# Revit family: QUADRATE NEON FLEX 1312_NDFX35_UU.1_N.1
name_source: partatom
category: Luminarias
units: mm (PartAtom-declared; Revit-internal decimal feet)

## family parameters
Compartido = No
Corte con vacíos al cargar = No
Cota de conector redondo = Diámetro de uso
Origen de luz = Sí
Punto de cálculo de habitación = No
Se basa en plano de trabajo = Sí
Siempre vertical = No
Tipo de pieza = Normal

## types (1)
- QUADRATENEON FLEX 1312_NDFX35.UU.1
    Cambio de temperatura de color de luz atenuada = <Ninguno>
    Comentarios de vataje = 24
    Descripción = MANGUERA LUMINOSA QUADRATE NEON FLEX DE PLASTICO FLEXIBLE CON UNA POTENCIA DE 10.6W/M, USO PARA EXTERIORES IP67, IRC 80, IK 08, TEMPERATURA EN BLANCO ULTRA CALIDO 2300K, 640 LUMENES/M, PRESENTACION DE 5-10M, CORTE 5CM, ALIMENTADO A 24V, REQUIERE ACCESORIOS.
    Elevación por defecto = 0 mm  [stored 0 ft]
    Fabricante = BRILLANT
    Filtro de color = 16777215
    Longitud de línea de emisión = 600 mm
    Marca = BRILLANT
    Modelo = NDFX35.UU.1
    Modelo Lampara = 2835 SMD
    Tamaño de símbolo de origen de luz = 610 mm

note: [stored X ft] marks values corroborated as IEEE doubles in the binary element streams (Revit-internal decimal feet)

## geometry (parser evidence)
native form markers: Blend x2
no freeform markers — native parametric forms only
